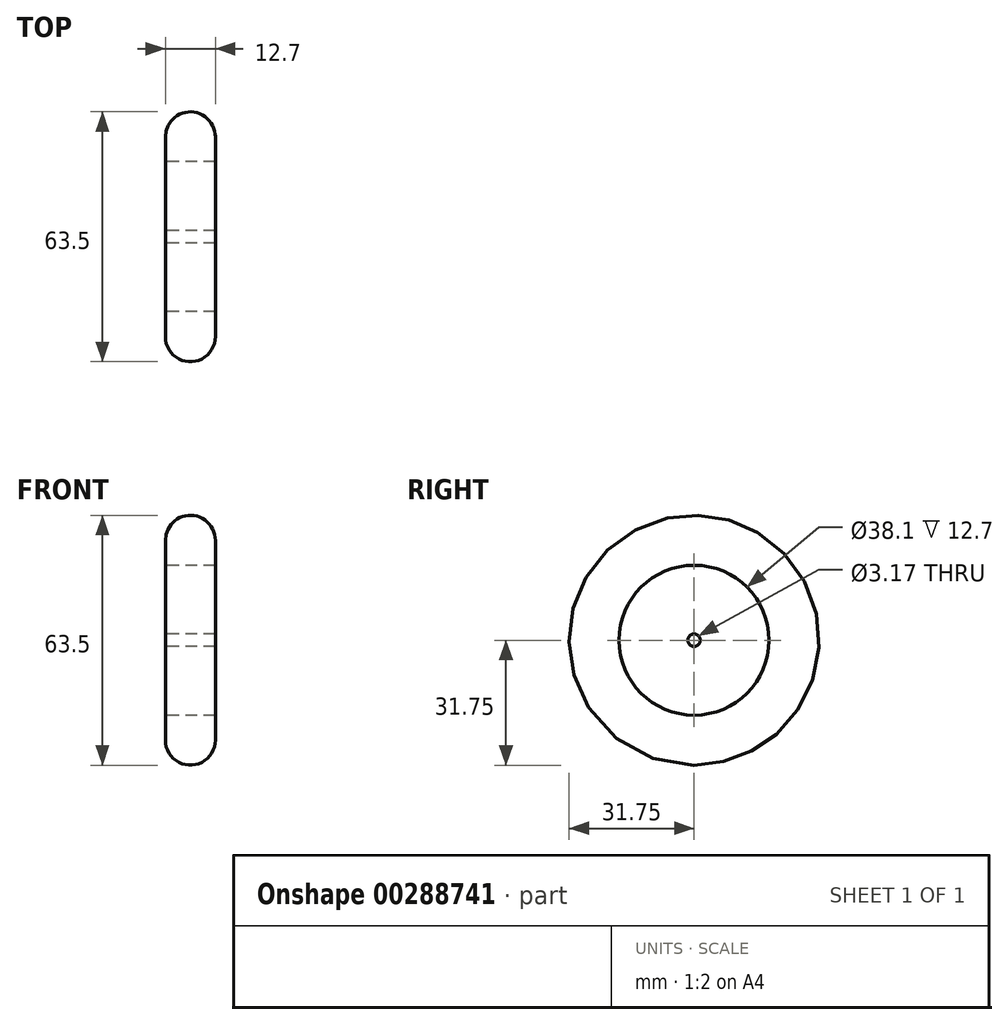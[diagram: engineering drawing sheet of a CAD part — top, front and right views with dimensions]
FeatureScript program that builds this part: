
annotation { "Feature Type Name" : "Feature", "Feature Type Description" : "" }
export const myFeature = defineFeature(function(context is Context, id is Id, definition is map)
    precondition{}
    {
        {
            var Q0;
            Q0=qCreatedBy(makeId("Right.planeOp"),FACE);
            var sketch = newSketch(context, id + "F0", { "sketchPlane" : qUnion([Q0])});
            skCircle(sketch, "E0", {"center": v(0, 0) * mm, "radius": 1.59 * mm});
            skCircle(sketch, "E1", {"center": v(0, 0) * mm, "radius": 19.05 * mm});
            skCircle(sketch, "E2", {"center": v(0, 0) * mm, "radius": 31.75 * mm});
            skSolve(sketch);
        }
        {
            var Q0;
            Q0=makeQuery(id+"F0.imprint","IMPRINT",FACE,{"disambiguationData":[TD([[makeQuery(id+"F0.imprint","IMPRINT",EDGE,{"derivedFrom":sQuery(id+"F0.wireOp",EDGE,"E0")}),-1.0]])]});
            extrude(context, id + "F1", {"entities" : qUnion([Q0]), "endBound" : BoundingType.SYMMETRIC, "depth" : 12.7 * mm});
        }
        {
            var Q0;
            Q0=makeQuery(id+"F0.imprint","IMPRINT",FACE,{"disambiguationData":[TD([[makeQuery(id+"F0.imprint","IMPRINT",EDGE,{"derivedFrom":sQuery(id+"F0.wireOp",EDGE,"E1")}),-1.0]])]});
            extrude(context, id + "F2", {"entities" : qUnion([Q0]), "endBound" : BoundingType.SYMMETRIC, "depth" : 12.7 * mm});
        }
        {
            var Q0;
            Q0=makeQuery(id+"F2.opExtrude","CAP_EDGE",EDGE,{"disambiguationData":[OSD([sQuery(id+"F0.wireOp",EDGE,"E2")])],"isStart":false});
            var Q1;
            Q1=makeQuery(id+"F2.opExtrude","CAP_EDGE",EDGE,{"disambiguationData":[OSD([sQuery(id+"F0.wireOp",EDGE,"E2")])],"isStart":true});
            fillet(context, id + "F3", {"entities" : qUnion([Q0, Q1]), "radius" : 6.35 * mm, "tangentPropagation" : true, "allowEdgeOverflow" : false});
        }
    });
